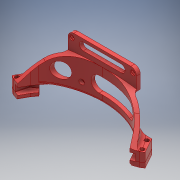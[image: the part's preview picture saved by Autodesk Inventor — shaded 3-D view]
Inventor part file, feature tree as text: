
AUTODESK INVENTOR PART (.ipt)
format: ipt  version: 2017 (Build 210142000, 142)  size: 1,261,568 bytes
history: native  units: mm
features: extrude x12, other x11, projected_geometry x11, sketch x11, plane x4, fillet x4, reference x4, chamfer x3, hole x3, mirror x2
ambient origin geometry x8: Origin, YZ Plane, XZ Plane, XY Plane, X Axis, Y Axis, Z Axis, Center Point
bodies: Body1 (feature_tree), Body2 (feature_tree), Body3 (feature_tree)
feature tree (65):
  other  "core"
  extrude  "Extrusion1"  Depth=12.0mm
  extrude  "Extrusion2"  Depth=18.0mm
  extrude  "Extrusion3"  Depth=17.453293mm
  chamfer  "Chamfer1"  Distance=5.0mm
  hole  "Hole1"  [1 undecoded]
  hole  "Hole2"  [1 undecoded]
  plane  "Work Plane1"
  extrude  "Extrusion4"  Depth=4.0mm
  extrude  "Extrusion5"  Depth=46.25mm TaperAngle=0.0deg
  extrude  "Extrusion6"  Depth=10.0mm TaperAngle=0.0deg
  extrude  "Extrusion11"  Depth=46.25mm
  mirror  "Mirror1"
  extrude  "Extrusion13"  Depth=46.25mm TaperAngle=0.0deg
  chamfer  "Chamfer4"  Distance=4.0mm
  plane  "Work Plane3"
  mirror  "Mirror2"
  fillet  "Fillet2"  Radius=2.0mm
  chamfer  "Chamfer3"  Distance=0.65mm
  plane  "Work Plane7"
  extrude  "Extrusion19"  Depth=46.25mm TaperAngle=45.0deg
  hole  "Hole8"  [1 undecoded]
  fillet  "Fillet10"  Radius=4.05mm
  fillet  "Fillet11"  Radius=64.0mm
  extrude  "Extrusion20"  Depth=46.25mm
  plane  "Work Plane8"
  extrude  "Extrusion21"  Depth=46.25mm
  extrude  "Extrusion22"  Depth=46.25mm
  fillet  "Fillet12"  Radius=5.0mm
  reference  "Reference1"
  reference  "Reference2"
  projected_geometry  "Projected Loop1"
  sketch  "Sketch3"  dims[d1=8.0mm d2=12.0mm]
  projected_geometry  "Projected Loop2"
  other  "clamp_r"
  sketch  "Sketch4"  dims[d3=3.0mm d4=0.0mm d5=18.0mm]
  projected_geometry  "Projected Loop3"
  sketch  "Sketch5"  dims[d6=6.5mm d7=0.0mm d8=17.453293mm]
  reference  "Reference3"
  projected_geometry  "Projected Loop4"
  projected_geometry  "Projected Loop5"
  sketch  "Sketch8"  dims[d9=16.0mm]
  other  "Pattern of core:1"
  other  "clamp_l"
  sketch  "Sketch15"  dims[d10=6.0mm d11=5.0mm d12=0.0mm]
  projected_geometry  "Projected Loop10"
  sketch  "Sketch17"  dims[d13=1.5mm d14=2.0mm d15=45.0deg d19=12.0mm]
  projected_geometry  "Projected Loop12"
  sketch  "Sketch25"  dims[d20=4.0mm d21=3.0mm]
  projected_geometry  "Projected Loop19"
  projected_geometry  "Projected Loop20"
  projected_geometry  "Projected Loop21"
  projected_geometry  "Projected Loop22"
  sketch  "Sketch26"  dims[d22=3.0mm]
  sketch  "Sketch27"  dims[d23=2.2mm d24=6.0mm d25=4.0mm d26=2.0mm d27=90.0deg d28=8.0mm d29=20.594885mm]
  reference  "Reference7"
  sketch  "Sketch28"  dims[d30=2.2mm d31=6.0mm d32=4.0mm d33=2.0mm d34=90.0deg d35=8.0mm d36=20.594885mm d38=4.0mm]
  sketch  "Sketch29"  dims[d39=3.0mm d40=0.0mm d41=30.0mm d42=0.0mm d43=10.0mm d44=0.0mm d89=4.05mm d91=4.0mm d92=0.0mm d94=4.0mm d95=2.0mm d96=2.0mm d97=45.0deg d100=0.65mm d101=0.0mm d102=1.2mm d103=2.0mm d104=45.0deg d118=1.8mm d166=4.05mm d167=64.0mm d168=12.5mm d169=33.0mm d170=72.0mm d171=5.0mm d172=3.25mm d173=0.0mm d174=33.0mm d175=5.0mm d176=64.0mm d177=2.3mm d178=6.0mm d179=4.0mm d180=2.0mm d181=90.0deg d182=8.0mm d183=20.594885mm d184=12.5mm d185=12.0mm d186=5.0mm d187=4.0mm d188=6.0mm d189=6.0mm d190=3.25mm d191=0.0mm d192=34.0mm d193=34.0mm d194=16.394811mm d195=16.394811mm d196=16.0mm d197=8.0mm d198=3.0mm d199=40.0mm d200=6.0mm d201=5.0mm d202=5.0mm d203=5.0mm d204=7.0mm d205=0.0mm d206=4.05mm d207=4.05mm d208=4.05mm d209=1.6mm d210=0.0mm d211=46.25mm]
  other  "<userpath>\Dropbox\Work\HeadSLAM\xtion_custom_assembly.iam"
  other  "xtion_custom_assembly.iam"
  other  "pupil_frame_full:1"
  other  "<userpath>\Dropbox\Work\HeadSLAM\xtion_custom_assembly_v3_FULL.iam"
  other  "xtion_custom_assembly_v3_FULL.iam"
  other  "xtion_heatsink_mount_FULL:1"
  other  "<userpath>\Dropbox\Work\HeadSLAM\xtion_custom_assembly.iam"
note: 3 required parameter values undecoded (feature->parameter linkage not recoverable at this tier; creation-order binding heuristic only, values carry confidence <= 0.55)
